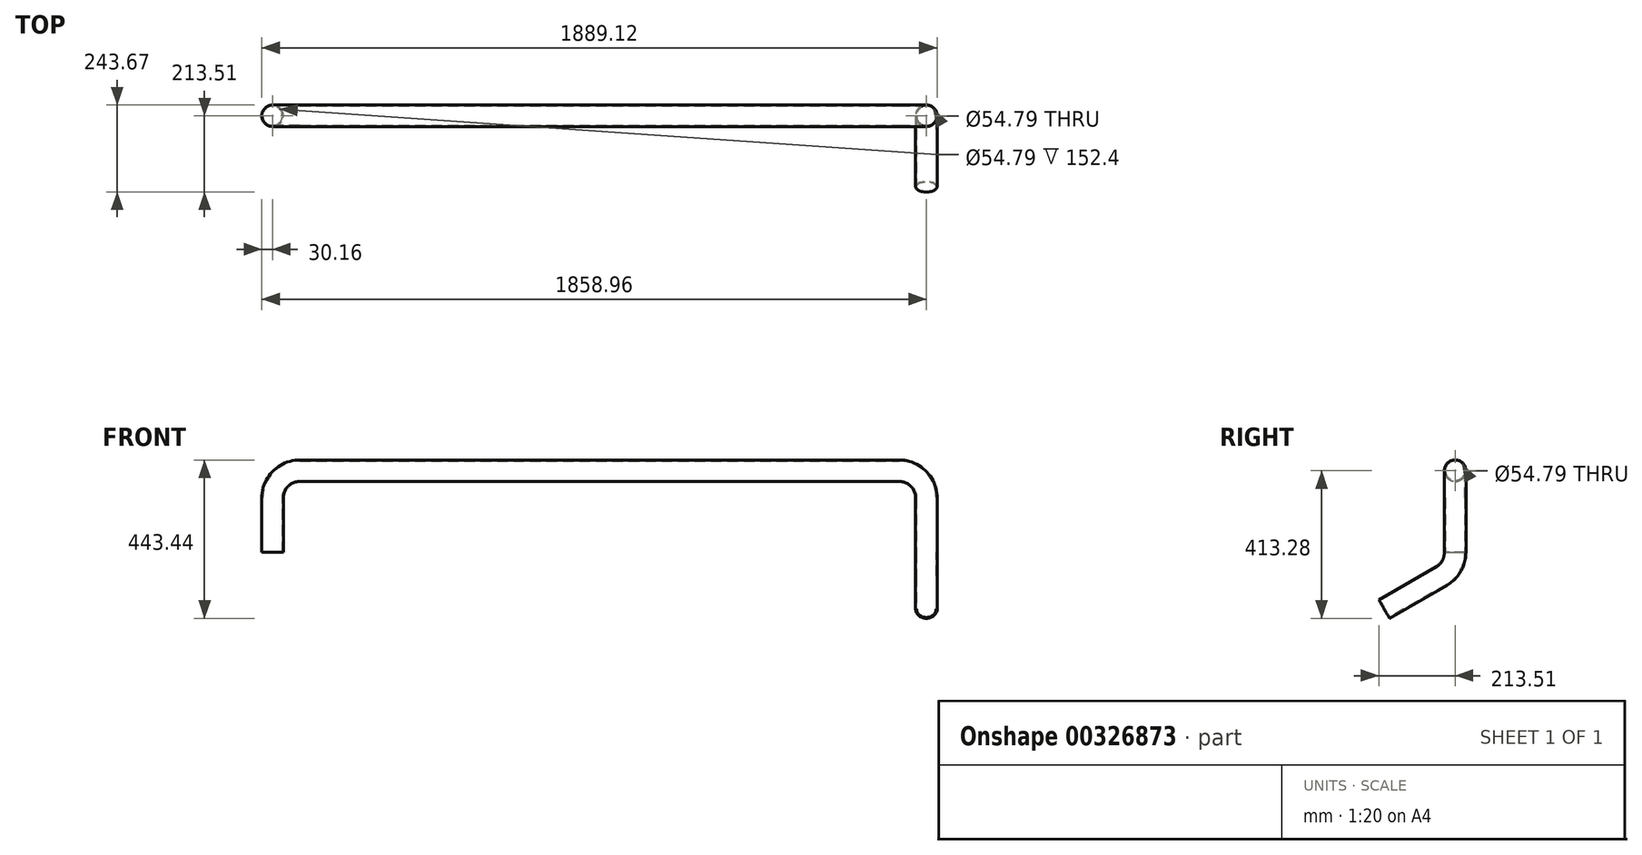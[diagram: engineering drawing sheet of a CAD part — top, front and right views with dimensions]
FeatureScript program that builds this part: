
annotation { "Feature Type Name" : "Feature", "Feature Type Description" : "" }
export const myFeature = defineFeature(function(context is Context, id is Id, definition is map)
    precondition{}
    {
        {
            var Q0;
            Q0=qCreatedBy(makeId("Front.planeOp"),FACE);
            var sketch = newSketch(context, id + "F0", { "sketchPlane" : qUnion([Q0])});
            skLineSegment(sketch, "E0", {"start": v(0, 0) * mm, "end": v(0, 152.4) * mm});
            skLineSegment(sketch, "E1", {"start": v(76.2, 228.6) * mm, "end": v(1752.6, 228.6) * mm});
            skLineSegment(sketch, "E2", {"start": v(1828.8, 152.4) * mm, "end": v(1828.8, 0) * mm});
            skPoint(sketch, "E3.visualSharp", {"position": v(0, 228.6) * mm});
            skArc(sketch, "E3.filletArc", {"start": v(76.2, 228.6) * mm, "mid": v(22.32, 206.28) * mm, "end": v(0, 152.4) * mm});
            skPoint(sketch, "E4.visualSharp", {"position": v(1828.8, 228.6) * mm});
            skArc(sketch, "E4.filletArc", {"start": v(1828.8, 152.4) * mm, "mid": v(1806.48, 206.28) * mm, "end": v(1752.6, 228.6) * mm});
            skSolve(sketch);
        }
        {
            var Q0;
            Q0=qCreatedBy(makeId("Top.planeOp"),FACE);
            var sketch = newSketch(context, id + "F1", { "sketchPlane" : qUnion([Q0])});
            skCircle(sketch, "E5", {"center": v(0, 0) * mm, "radius": 30.16 * mm});
            skCircle(sketch, "E6", {"center": v(0, 0) * mm, "radius": 27.4 * mm});
            skSolve(sketch);
        }
        {
            var Q0;
            Q0=qCreatedBy(makeId("Right.planeOp"),FACE);
            var Q1;
            Q1=sQuery(id+"F0.wireOp",VERTEX,"E2.end");
            cPlane(context, id + "F2", {"entities" : qUnion([Q0, Q1]), "cplaneType" : CPlaneType.PLANE_POINT, "offset" : 25.4 * mm, "width" : 152.4 * mm, "height" : 152.4 * mm});
        }
        {
            var Q0;
            Q0=qCreatedBy(id+"F2.planeOp",FACE);
            var sketch = newSketch(context, id + "F3", { "sketchPlane" : qUnion([Q0])});
            skArc(sketch, "E7", {"start": v(-38.1, -66) * mm, "mid": v(-10.2, -38.1) * mm, "end": v(0, 0) * mm});
            skLineSegment(sketch, "E8", {"start": v(-38.1, -66) * mm, "end": v(-198.43, -158.56) * mm});
            skPoint(sketch, "E9", {"position": v(0, 0) * mm});
            skSolve(sketch);
        }
        {
            var Q0;
            Q0 = qSketchRegion(id + "F1", true);
            var Q1;
            Q1 = qConstructionFilter(qBodyType(qCreatedBy(id + "F0" ,EDGE), BodyType.WIRE), ConstructionObject.NO);
            var Q2;
            Q2 = qConstructionFilter(qBodyType(qCreatedBy(id + "F3" ,EDGE), BodyType.WIRE), ConstructionObject.NO);
            sweep(context, id + "F4", {"profiles" : qUnion([Q0]), "path" : qUnion([Q1, Q2])});
        }
    });
